# Revit family: 696RG3021_3 Outlet_w_Dual Arrester
name_source: partatom
category: Plumbing Fixtures
units: mm (PartAtom-declared; Revit-internal decimal feet)

## family parameters
Cut with Voids When Loaded = No
Host = Face
Part Type = Normal
Room Calculation Point = No
Round Connector Dimension = Use Diameter
Shared = No

## types (10) — shared parameters
Default Elevation = 40 "
Description = Three Quarter Turn arrester Vavles
Manufacturer = Sioux Chief
Outlet Connector Type = 1/4", 3/8" Compression
URL = www.siouxchief.com
Waste Connection = No

## per-type parameters (varying)
| type | Inlet Connector Type | Keynote | Model |
| 696-G3021MR (MIP/Female Sweat) | MIP/Female Sweat |  | 696-G3021MR |
| 696-G3021WR (ASTM F1960 PEX) | ASTM F1960 PEX |  | 696-G3021WR |
| 696-G3021XR (ASTM F1807 PEX) | ASTM F1807 PEX |  | 696-G3021XR |
| 696-G3021CR (CPVC Male) | CPVC Male |  | 696-G3021CR |
| 696-G3021PR (Male Sweat/Copper Press) | Male Sweat/Copper Press |  | 696-G3021PR |
| 696RG3021MF (MIP/Female Sweat) | MIP/Female Sweat | Fire Rated | 696RG3021MF |
| 696RG3021WF (ASTM F1960 PEX) | ASTM F1960 PEX | Fire Rated | 696RG3021WF |
| 696RG3021XF (ASTM F1807 PEX) | ASTM F1807 PEX | Fire Rated | 696RG3021XF |
| 696RG3021CF (CPVC Male) | CPVC Male | Fire Rated | 696RG3021CF |
| 696RG3021PF (Male Sweat/Copper Press) | Male Sweat/Copper Press | Fire Rated | 696RG3021PF |

## geometry (parser evidence)
native form markers: Sweep x2
no freeform markers — native parametric forms only
